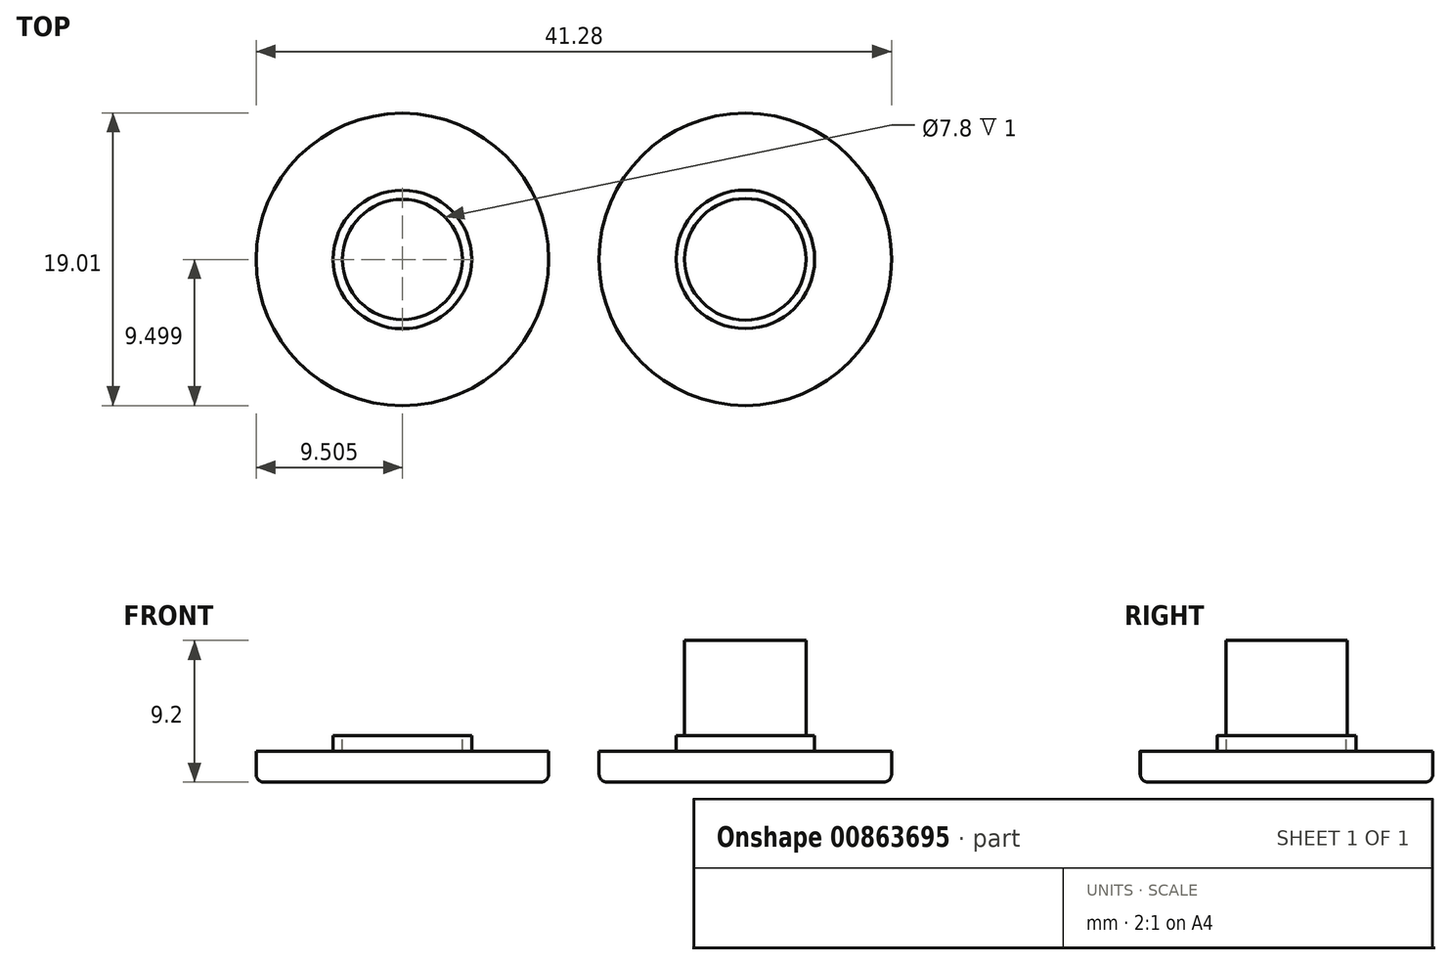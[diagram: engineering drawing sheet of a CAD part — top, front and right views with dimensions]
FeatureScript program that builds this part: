
annotation { "Feature Type Name" : "Feature", "Feature Type Description" : "" }
export const myFeature = defineFeature(function(context is Context, id is Id, definition is map)
    precondition{}
    {
        {
            var Q0;
            Q0=qCreatedBy(makeId("Top.planeOp"),FACE);
            var sketch = newSketch(context, id + "F0", { "sketchPlane" : qUnion([Q0])});
            skCircle(sketch, "E0", {"center": v(0, 0) * mm, "radius": 9.5 * mm});
            skSolve(sketch);
        }
        {
            var Q0;
            Q0 = qSketchRegion(id + "F0", true);
            extrude(context, id + "F1", {"entities" : qUnion([Q0]), "depth" : 2 * mm, "offsetDistance" : 25 * mm});
        }
        {
            var Q0;
            Q0=makeQuery(id+"F1.opExtrude","CAP_EDGE",EDGE,{"disambiguationData":[OSD([sQuery(id+"F0.wireOp",EDGE,"E0")])],"isStart":true});
            fillet(context, id + "F2", {"entities" : qUnion([Q0]), "radius" : .5 * mm, "tangentPropagation" : true, "allowEdgeOverflow" : false});
        }
        {
            var Q0;
            Q0=makeQuery(id+"F1.opExtrude","CAP_FACE",FACE,{"disambiguationData":[OSD([sQuery(id+"F0.wireOp",EDGE,"E0")])],"isStart":false});
            var sketch = newSketch(context, id + "F3", { "sketchPlane" : qUnion([Q0])});
            skCircle(sketch, "E1", {"center": v(0, 0) * mm, "radius": 4.5 * mm});
            skSolve(sketch);
        }
        {
            var Q0;
            Q0=makeQuery(id+"F3.imprint","IMPRINT",FACE,{"disambiguationData":[TD([[makeQuery(id+"F3.imprint","IMPRINT",EDGE,{"derivedFrom":sQuery(id+"F3.wireOp",EDGE,"E1")}),1.0]])]});
            extrude(context, id + "F4", {"entities" : qUnion([Q0]), "operationType" : NewBodyOperationType.ADD, "depth" : 1 * mm, "offsetDistance" : 25 * mm});
        }
        {
            var Q0;
            Q0=makeQuery(id+"F4.opExtrude","CAP_FACE",FACE,{"disambiguationData":[OSD([sQuery(id+"F3.wireOp",EDGE,"E1")])],"isStart":false});
            var sketch = newSketch(context, id + "F5", { "sketchPlane" : qUnion([Q0])});
            skCircle(sketch, "E2", {"center": v(0, 0) * mm, "radius": 3.95 * mm});
            skSolve(sketch);
        }
        {
            var Q0;
            Q0=makeQuery(id+"F5.imprint","IMPRINT",FACE,{"disambiguationData":[TD([[makeQuery(id+"F5.imprint","IMPRINT",EDGE,{"derivedFrom":sQuery(id+"F5.wireOp",EDGE,"E2")}),1.0]])]});
            extrude(context, id + "F6", {"entities" : qUnion([Q0]), "operationType" : NewBodyOperationType.ADD, "depth" : 6.2 * mm, "offsetDistance" : 25 * mm});
        }
        {
            var Q0;
            Q0=qCreatedBy(makeId("Top.planeOp"),FACE);
            var sketch = newSketch(context, id + "F7", { "sketchPlane" : qUnion([Q0])});
            skCircle(sketch, "E3", {"center": v(-41.08, 31.59) * mm, "radius": 9.5 * mm});
            skSolve(sketch);
        }
        {
            var Q0;
            Q0=makeQuery(id+"F7.imprint","IMPRINT",FACE,{"disambiguationData":[TD([[makeQuery(id+"F7.imprint","IMPRINT",EDGE,{"derivedFrom":sQuery(id+"F7.wireOp",EDGE,"E3")}),1.0]])]});
            extrude(context, id + "F8", {"entities" : qUnion([Q0]), "depth" : 2 * mm, "offsetDistance" : 25 * mm});
        }
        {
            var Q0;
            Q0=makeQuery(id+"F8.opExtrude","CAP_EDGE",EDGE,{"disambiguationData":[OSD([sQuery(id+"F7.wireOp",EDGE,"E3")])],"isStart":true});
            fillet(context, id + "F9", {"entities" : qUnion([Q0]), "radius" : .5 * mm, "tangentPropagation" : true, "allowEdgeOverflow" : false});
        }
        {
            var Q0;
            Q0=makeQuery(id+"F8.opExtrude","CAP_FACE",FACE,{"disambiguationData":[OSD([sQuery(id+"F7.wireOp",EDGE,"E3")])],"isStart":false});
            var sketch = newSketch(context, id + "F10", { "sketchPlane" : qUnion([Q0])});
            skCircle(sketch, "E4", {"center": v(-41.08, 31.59) * mm, "radius": 4.5 * mm});
            skSolve(sketch);
        }
        {
            var Q0;
            Q0=makeQuery(id+"F10.imprint","IMPRINT",FACE,{"disambiguationData":[TD([[makeQuery(id+"F10.imprint","IMPRINT",EDGE,{"derivedFrom":sQuery(id+"F10.wireOp",EDGE,"E4")}),1.0]])]});
            extrude(context, id + "F11", {"entities" : qUnion([Q0]), "operationType" : NewBodyOperationType.ADD, "depth" : 1 * mm, "offsetDistance" : 25 * mm});
        }
        {
            var Q0;
            Q0=makeQuery(id+"F11.opExtrude","CAP_FACE",FACE,{"disambiguationData":[OSD([sQuery(id+"F10.wireOp",EDGE,"E4")])],"isStart":false});
            var sketch = newSketch(context, id + "F12", { "sketchPlane" : qUnion([Q0])});
            skCircle(sketch, "E5", {"center": v(-41.08, 31.59) * mm, "radius": 3.9 * mm});
            skSolve(sketch);
        }
        {
            var Q0;
            Q0=makeQuery(id+"F12.imprint","IMPRINT",FACE,{"disambiguationData":[TD([[makeQuery(id+"F12.imprint","IMPRINT",EDGE,{"derivedFrom":sQuery(id+"F12.wireOp",EDGE,"E5")}),1.0]])]});
            extrude(context, id + "F13", {"entities" : qUnion([Q0]), "operationType" : NewBodyOperationType.REMOVE, "oppositeDirection" : true, "depth" : 1 * mm, "offsetDistance" : 25 * mm});
        }
        {
            var Q0;
            Q0=makeQuery(id+"F8.opExtrude","SWEPT_BODY",BODY,{"disambiguationData":[OSD([sQuery(id+"F7.wireOp",EDGE,"E3")])]});
            var Q1;
            Q1=qCreatedBy(makeId("Front.planeOp"),FACE);
            transform(context, id + "F14", {"entities" : qUnion([Q0]), "transformType" : TransformType.TRANSLATION_DISTANCE, "transformDirection" : qUnion([Q1]), "distance" : 31 * mm, "makeCopy" : false});
        }
        {
            var Q0;
            Q0=makeQuery(id+"F8.opExtrude","SWEPT_BODY",BODY,{"disambiguationData":[OSD([sQuery(id+"F7.wireOp",EDGE,"E3")])]});
            transform(context, id + "F15", {"entities" : qUnion([Q0]), "transformType" : TransformType.TRANSLATION_3D, "dx" : 18.8 * mm, "dy" : -0.6 * mm, "dz" : 0 * mm, "makeCopy" : false});
        }
    });
